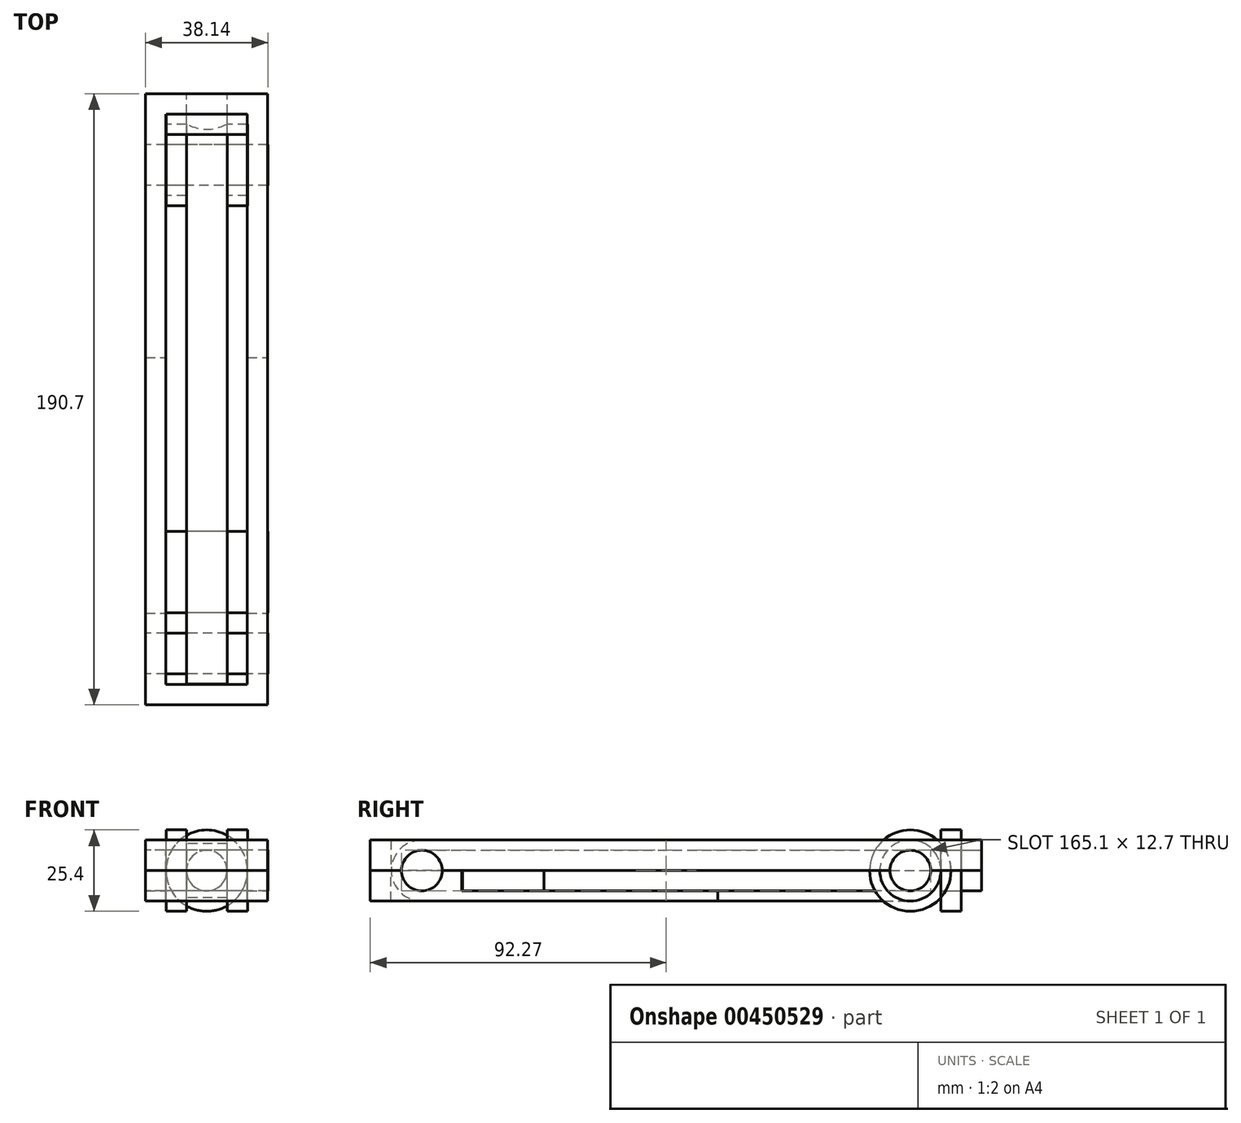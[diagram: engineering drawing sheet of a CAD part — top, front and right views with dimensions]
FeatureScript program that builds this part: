
annotation { "Feature Type Name" : "Feature", "Feature Type Description" : "" }
export const myFeature = defineFeature(function(context is Context, id is Id, definition is map)
    precondition{}
    {
        {
            var Q0;
            Q0=qCreatedBy(makeId("Front.planeOp"),FACE);
            cPlane(context, id + "F0", {"entities" : qUnion([Q0]), "cplaneType" : CPlaneType.OFFSET, "offset" : 28.57 * mm, "width" : 152.4 * mm, "height" : 152.4 * mm});
        }
        {
            var Q0;
            Q0=qCreatedBy(id+"F0.planeOp",FACE);
            var sketch = newSketch(context, id + "F1", { "sketchPlane" : qUnion([Q0])});
            skPoint(sketch, "E0.0", {"position": v(0, 0) * mm});
            skLineSegment(sketch, "E1", {"start": v(0, 0) * mm, "end": v(0, -25.4) * mm});
            skCircle(sketch, "E2", {"center": v(0, -25.4) * mm, "radius": 12.7 * mm});
            skCircle(sketch, "E3", {"center": v(0, -25.4) * mm, "radius": 6.35 * mm});
            skSolve(sketch);
        }
        {
            var Q0;
            Q0 = qSketchRegion(id + "F1", true);
            extrude(context, id + "F2", {"entities" : qUnion([Q0]), "depth" : 6.35 * mm});
        }
        {
            var Q0;
            Q0=qCreatedBy(makeId("Right.planeOp"),FACE);
            var sketch = newSketch(context, id + "F3", { "sketchPlane" : qUnion([Q0])});
            skLineSegment(sketch, "E4", {"start": v(0, 0) * mm, "end": v(0, -25.4) * mm});
            skLineSegment(sketch, "E5", {"start": v(0, -25.4) * mm, "end": v(-44.45, -25.4) * mm});
            skCircle(sketch, "E6", {"center": v(-44.45, -25.4) * mm, "radius": 12.7 * mm});
            skCircle(sketch, "E7", {"center": v(-44.45, -25.4) * mm, "radius": 6.35 * mm});
            skCircle(sketch, "E8", {"center": v(-44.45, -25.4) * mm, "radius": 9.53 * mm});
            skSolve(sketch);
        }
        {
            var Q0;
            Q0=makeQuery(id+"F3.imprint","IMPRINT",FACE,{"disambiguationData":[TD([[makeQuery(id+"F3.imprint","IMPRINT",EDGE,{"derivedFrom":sQuery(id+"F3.wireOp",EDGE,"E6")}),1.0]])]});
            extrude(context, id + "F4", {"entities" : qUnion([Q0]), "depth" : 25.4 * mm, "symmetric" : true});
        }
        {
            var Q0;
            Q0 = qSketchRegion(id + "F3", true);
            var Q1;
            Q1=sQuery(id+"F3.wireOp",EDGE,"E6");
            extrude(context, id + "F5", {"entities" : qUnion([Q0]), "operationType" : NewBodyOperationType.REMOVE, "surfaceEntities" : qUnion([Q1]), "depth" : 12.7 * mm, "symmetric" : true});
        }
        {
            var Q0;
            Q0=makeQuery(id+"F3.imprint","IMPRINT",FACE,{"disambiguationData":[TD([[makeQuery(id+"F3.imprint","IMPRINT",EDGE,{"derivedFrom":sQuery(id+"F3.wireOp",EDGE,"E7")}),1.0]])]});
            extrude(context, id + "F6", {"entities" : qUnion([Q0]), "depth" : 38.1 * mm, "symmetric" : true});
        }
        {
            var Q0;
            Q0=makeQuery(id+"F3.imprint","IMPRINT",FACE,{"disambiguationData":[TD([[makeQuery(id+"F3.imprint","IMPRINT",EDGE,{"derivedFrom":sQuery(id+"F3.wireOp",EDGE,"E7")}),-1.0]])]});
            extrude(context, id + "F7", {"entities" : qUnion([Q0]), "depth" : 25.4 * mm, "symmetric" : true});
        }
        {
            var Q0;
            Q0=makeQuery(id+"F3.imprint","IMPRINT",FACE,{"disambiguationData":[TD([[makeQuery(id+"F3.imprint","IMPRINT",EDGE,{"derivedFrom":sQuery(id+"F3.wireOp",EDGE,"E7")}),-1.0]])]});
            extrude(context, id + "F8", {"entities" : qUnion([Q0]), "operationType" : NewBodyOperationType.REMOVE, "depth" : 12.7 * mm, "symmetric" : true});
        }
        {
            var Q0;
            Q0=qCreatedBy(makeId("Right.planeOp"),FACE);
            var sketch = newSketch(context, id + "F9", { "sketchPlane" : qUnion([Q0])});
            skCircle(sketch, "E9.0.0", {"center": v(-44.45, -25.4) * mm, "radius": 6.35 * mm});
            skArc(sketch, "E10.0.0", {"start": v(-44.45, -34.92) * mm, "mid": v(-34.93, -25.4) * mm, "end": v(-44.45, -15.88) * mm});
            skLineSegment(sketch, "E11", {"start": v(-44.45, -15.88) * mm, "end": v(-196.85, -15.88) * mm});
            skArc(sketch, "E12", {"start": v(-196.85, -15.88) * mm, "mid": v(-206.38, -25.4) * mm, "end": v(-196.85, -34.92) * mm});
            skCircle(sketch, "E13", {"center": v(-196.85, -25.4) * mm, "radius": 6.35 * mm});
            skLineSegment(sketch, "E14", {"start": v(-196.85, -34.92) * mm, "end": v(-44.45, -34.92) * mm});
            skLineSegment(sketch, "E15", {"start": v(-196.85, -19.05) * mm, "end": v(-44.45, -19.05) * mm});
            skLineSegment(sketch, "E16", {"start": v(-44.45, -31.75) * mm, "end": v(-196.85, -31.75) * mm});
            skLineSegment(sketch, "E17.bottom", {"start": v(-184.15, -25.4) * mm, "end": v(-158.75, -25.4) * mm});
            skLineSegment(sketch, "E17.top", {"start": v(-184.15, -31.75) * mm, "end": v(-158.75, -31.75) * mm});
            skLineSegment(sketch, "E17.left", {"start": v(-184.15, -25.4) * mm, "end": v(-184.15, -31.75) * mm});
            skLineSegment(sketch, "E17.right", {"start": v(-158.75, -25.4) * mm, "end": v(-158.75, -31.75) * mm});
            skLineSegment(sketch, "E18.bottom", {"start": v(-184.15, -34.92) * mm, "end": v(-158.75, -34.92) * mm});
            skLineSegment(sketch, "E18.top", {"start": v(-184.15, -41.27) * mm, "end": v(-158.75, -41.27) * mm});
            skLineSegment(sketch, "E18.left", {"start": v(-184.15, -34.92) * mm, "end": v(-184.15, -41.27) * mm});
            skLineSegment(sketch, "E18.right", {"start": v(-158.75, -34.92) * mm, "end": v(-158.75, -41.27) * mm});
            skSolve(sketch);
        }
        {
            var Q0;
            Q0=makeQuery(id+"F9.imprint","IMPRINT",FACE,{"disambiguationData":[TD([[makeQuery(id+"F9.imprint","IMPRINT",EDGE,{"derivedFrom":sQuery(id+"F9.wireOp",EDGE,"E10.0.0")}),1.0]])]});
            extrude(context, id + "F10", {"entities" : qUnion([Q0]), "depth" : 12.7 * mm, "symmetric" : true});
        }
        {
            var Q0;
            {var subQ0=sQuery(id+"F9.wireOp",EDGE,"E13");var subQ1=makeQuery(id+"F9.imprint","INTERSECT",VERTEX,{"derivedFrom":[subQ0,sQuery(id+"F9.wireOp",EDGE,"E15")]});Q0=makeQuery(id+"F9.imprint","IMPRINT",FACE,{"disambiguationData":[TD([[makeQuery(id+"F9.imprint","IMPRINT",EDGE,{"disambiguationData":[TD([[subQ1,-1.0]])],"derivedFrom":subQ0}),1.0]])]});}
            extrude(context, id + "F11", {"entities" : qUnion([Q0]), "depth" : 38.1 * mm, "symmetric" : true});
        }
        {
            var Q0;
            Q0=makeQuery(id+"F9.imprint","IMPRINT",FACE,{"disambiguationData":[TD([[makeQuery(id+"F9.imprint","IMPRINT",EDGE,{"derivedFrom":sQuery(id+"F9.wireOp",EDGE,"E17.bottom")}),-1.0]])]});
            var Q1;
            Q1=makeQuery(id+"F9.imprint","IMPRINT",FACE,{"disambiguationData":[TD([[makeQuery(id+"F9.imprint","IMPRINT",EDGE,{"derivedFrom":sQuery(id+"F9.wireOp",EDGE,"E18.bottom")}),-1.0]])]});
            extrude(context, id + "F12", {"entities" : qUnion([Q0, Q1]), "depth" : 38.1 * mm, "symmetric" : true});
        }
        {
            var Q0;
            Q0=makeQuery(id+"F1.imprint","IMPRINT",FACE,{"disambiguationData":[TD([[makeQuery(id+"F1.imprint","IMPRINT",EDGE,{"derivedFrom":sQuery(id+"F1.wireOp",EDGE,"E3")}),1.0]])]});
            extrude(context, id + "F13", {"entities" : qUnion([Q0]), "depth" : 12.7 * mm, "symmetric" : true});
        }
        {
            var Q0;
            Q0=qCreatedBy(makeId("Top.planeOp"),FACE);
            cPlane(context, id + "F14", {"entities" : qUnion([Q0]), "cplaneType" : CPlaneType.OFFSET, "offset" : 25.4 * mm, "oppositeDirection" : true, "width" : 152.4 * mm, "height" : 152.4 * mm});
        }
        {
            var Q0;
            Q0=qCreatedBy(id+"F14.planeOp",FACE);
            var sketch = newSketch(context, id + "F15", { "sketchPlane" : qUnion([Q0])});
            skLineSegment(sketch, "E19", {"start": v(-19.09, -212.92) * mm, "end": v(19.01, -212.92) * mm});
            skLineSegment(sketch, "E20", {"start": v(-19.09, -22.23) * mm, "end": v(19.01, -22.22) * mm});
            skLineSegment(sketch, "E21", {"start": v(-19.09, -22.22) * mm, "end": v(-19.09, -212.92) * mm});
            skLineSegment(sketch, "E22", {"start": v(-12.73, -28.58) * mm, "end": v(-12.73, -206.56) * mm});
            skLineSegment(sketch, "E23", {"start": v(-12.73, -206.56) * mm, "end": v(12.67, -206.56) * mm});
            skLineSegment(sketch, "E24", {"start": v(12.67, -28.58) * mm, "end": v(12.67, -206.56) * mm});
            skLineSegment(sketch, "E25", {"start": v(19.01, -22.22) * mm, "end": v(19.01, -212.92) * mm});
            skLineSegment(sketch, "E26", {"start": v(-19.09, -212.92) * mm, "end": v(-19.09, -184.34) * mm});
            skLineSegment(sketch, "E27", {"start": v(-19.09, -184.34) * mm, "end": v(-12.73, -184.34) * mm});
            skLineSegment(sketch, "E28", {"start": v(-19.09, -184.34) * mm, "end": v(-19.09, -104.55) * mm});
            skLineSegment(sketch, "E29", {"start": v(-19.09, -104.55) * mm, "end": v(-12.73, -104.55) * mm});
            skLineSegment(sketch, "E30", {"start": v(12.67, -104.55) * mm, "end": v(19.01, -104.55) * mm});
            skLineSegment(sketch, "E31.trimOffspring", {"start": v(12.67, -184.34) * mm, "end": v(19.01, -184.34) * mm});
            skLineSegment(sketch, "E32.0", {"start": v(12.7, -28.58) * mm, "end": v(12.67, -28.58) * mm});
            skLineSegment(sketch, "E33", {"start": v(-12.7, -28.58) * mm, "end": v(-12.73, -28.58) * mm});
            skLineSegment(sketch, "E34", {"start": v(-12.7, -28.58) * mm, "end": v(12.67, -28.58) * mm});
            skSolve(sketch);
        }
        {
            var Q0;
            {var subQ5=sQuery(id+"F15.wireOp",EDGE,"E19");Q0=makeQuery(id+"F15.imprint","IMPRINT",FACE,{"disambiguationData":[TD([[makeQuery(id+"F15.imprint","IMPRINT",EDGE,{"derivedFrom":subQ5}),1.0]])]});}
            var Q1;
            {var subQ0=sQuery(id+"F15.wireOp",EDGE,"E27");Q1=makeQuery(id+"F15.imprint","IMPRINT",FACE,{"disambiguationData":[TD([[makeQuery(id+"F15.imprint","IMPRINT",EDGE,{"derivedFrom":subQ0}),1.0]])]});}
            var Q2;
            {var subQ1=sQuery(id+"F15.wireOp",EDGE,"5Luu25Ly-4ero-qbvc-7RJm-95hsiVW9VLKX");Q2=makeQuery(id+"F15.imprint","IMPRINT",FACE,{"disambiguationData":[TD([[makeQuery(id+"F15.imprint","IMPRINT",EDGE,{"derivedFrom":subQ1}),1.0]])]});}
            var Q3;
            {var subQ0=sQuery(id+"F15.wireOp",EDGE,"E30");Q3=makeQuery(id+"F15.imprint","IMPRINT",FACE,{"disambiguationData":[TD([[makeQuery(id+"F15.imprint","IMPRINT",EDGE,{"derivedFrom":subQ0}),-1.0]])]});}
            extrude(context, id + "F16", {"entities" : qUnion([Q0, Q1, Q2, Q3]), "oppositeDirection" : true, "depth" : 9.52 * mm});
        }
        {
            var Q0;
            {var subQ0=sQuery(id+"F15.wireOp",EDGE,"E27");Q0=makeQuery(id+"F15.imprint","IMPRINT",FACE,{"disambiguationData":[TD([[makeQuery(id+"F15.imprint","IMPRINT",EDGE,{"derivedFrom":subQ0}),1.0]])]});}
            var Q1;
            {var subQ0=sQuery(id+"F15.wireOp",EDGE,"E30");Q1=makeQuery(id+"F15.imprint","IMPRINT",FACE,{"disambiguationData":[TD([[makeQuery(id+"F15.imprint","IMPRINT",EDGE,{"derivedFrom":subQ0}),-1.0]])]});}
            extrude(context, id + "F17", {"entities" : qUnion([Q0, Q1]), "operationType" : NewBodyOperationType.REMOVE, "oppositeDirection" : true, "depth" : 6.35 * mm});
        }
        {
            var Q0;
            {var subQ0=sQuery(id+"F15.wireOp",EDGE,"E30");var subQ9=makeQuery(id+"F15.imprint","IMPRINT",EDGE,{"derivedFrom":subQ0});var subQ10=sQuery(id+"F15.wireOp",EDGE,"E27");var subQ18=makeQuery(id+"F15.imprint","IMPRINT",EDGE,{"derivedFrom":subQ10});var subQ21=sQuery(id+"F15.wireOp",EDGE,"E20");var subQ24=sQuery(id+"F15.wireOp",EDGE,"E19");Q0=qUnion([makeQuery(id+"F15.imprint","IMPRINT",FACE,{"disambiguationData":[TD([[makeQuery(id+"F15.imprint","IMPRINT",EDGE,{"derivedFrom":subQ24}),1.0]])]}),makeQuery(id+"F15.imprint","IMPRINT",FACE,{"disambiguationData":[TD([[makeQuery(id+"F15.imprint","IMPRINT",EDGE,{"derivedFrom":subQ21}),-1.0]])]}),makeQuery(id+"F15.imprint","IMPRINT",FACE,{"disambiguationData":[TD([[subQ18,1.0]])]}),makeQuery(id+"F15.imprint","IMPRINT",FACE,{"disambiguationData":[TD([[subQ9,-1.0]])]})]);}
            extrude(context, id + "F18", {"entities" : qUnion([Q0]), "depth" : 9.52 * mm});
        }
        {
            var Q0;
            Q0=makeQuery(id+"F11.opExtrude","SWEPT_BODY",BODY,{"disambiguationData":[OSD([sQuery(id+"F9.wireOp",EDGE,"E13")])]});
            var Q1;
            Q1=makeQuery(id+"F6.opExtrude","SWEPT_BODY",BODY,{"disambiguationData":[OSD([sQuery(id+"F3.wireOp",EDGE,"E7")])]});
            var Q2;
            Q2=makeQuery(id+"F13.opExtrude","SWEPT_BODY",BODY,{"disambiguationData":[OSD([sQuery(id+"F1.wireOp",EDGE,"E3")])]});
            var Q3;
            Q3=makeQuery(id+"F16.opExtrude","SWEPT_BODY",BODY,{"disambiguationData":[OSD([sQuery(id+"F15.wireOp",EDGE,"E19"),sQuery(id+"F15.wireOp",EDGE,"E21"),sQuery(id+"F15.wireOp",EDGE,"E22"),sQuery(id+"F15.wireOp",EDGE,"E23"),sQuery(id+"F15.wireOp",EDGE,"E24"),sQuery(id+"F15.wireOp",EDGE,"E25"),sQuery(id+"F15.wireOp",EDGE,"E29"),sQuery(id+"F15.wireOp",EDGE,"E30")])]});
            var Q4;
            Q4=makeQuery(id+"F18.opExtrude","SWEPT_BODY",BODY,{"disambiguationData":[OSD([sQuery(id+"F15.wireOp",EDGE,"E19"),sQuery(id+"F15.wireOp",EDGE,"E20"),sQuery(id+"F15.wireOp",EDGE,"E21"),sQuery(id+"F15.wireOp",EDGE,"E22"),sQuery(id+"F15.wireOp",EDGE,"E23"),sQuery(id+"F15.wireOp",EDGE,"E24"),sQuery(id+"F15.wireOp",EDGE,"E25"),sQuery(id+"F15.wireOp",EDGE,"E33"),sQuery(id+"F15.wireOp",EDGE,"E34")])]});
            booleanBodies(context, id + "F19", {"operationType" : BooleanOperationType.SUBTRACTION, "tools" : qUnion([Q0, Q1, Q2]), "targets" : qUnion([Q3, Q4]), "keepTools" : true});
        }
    });
